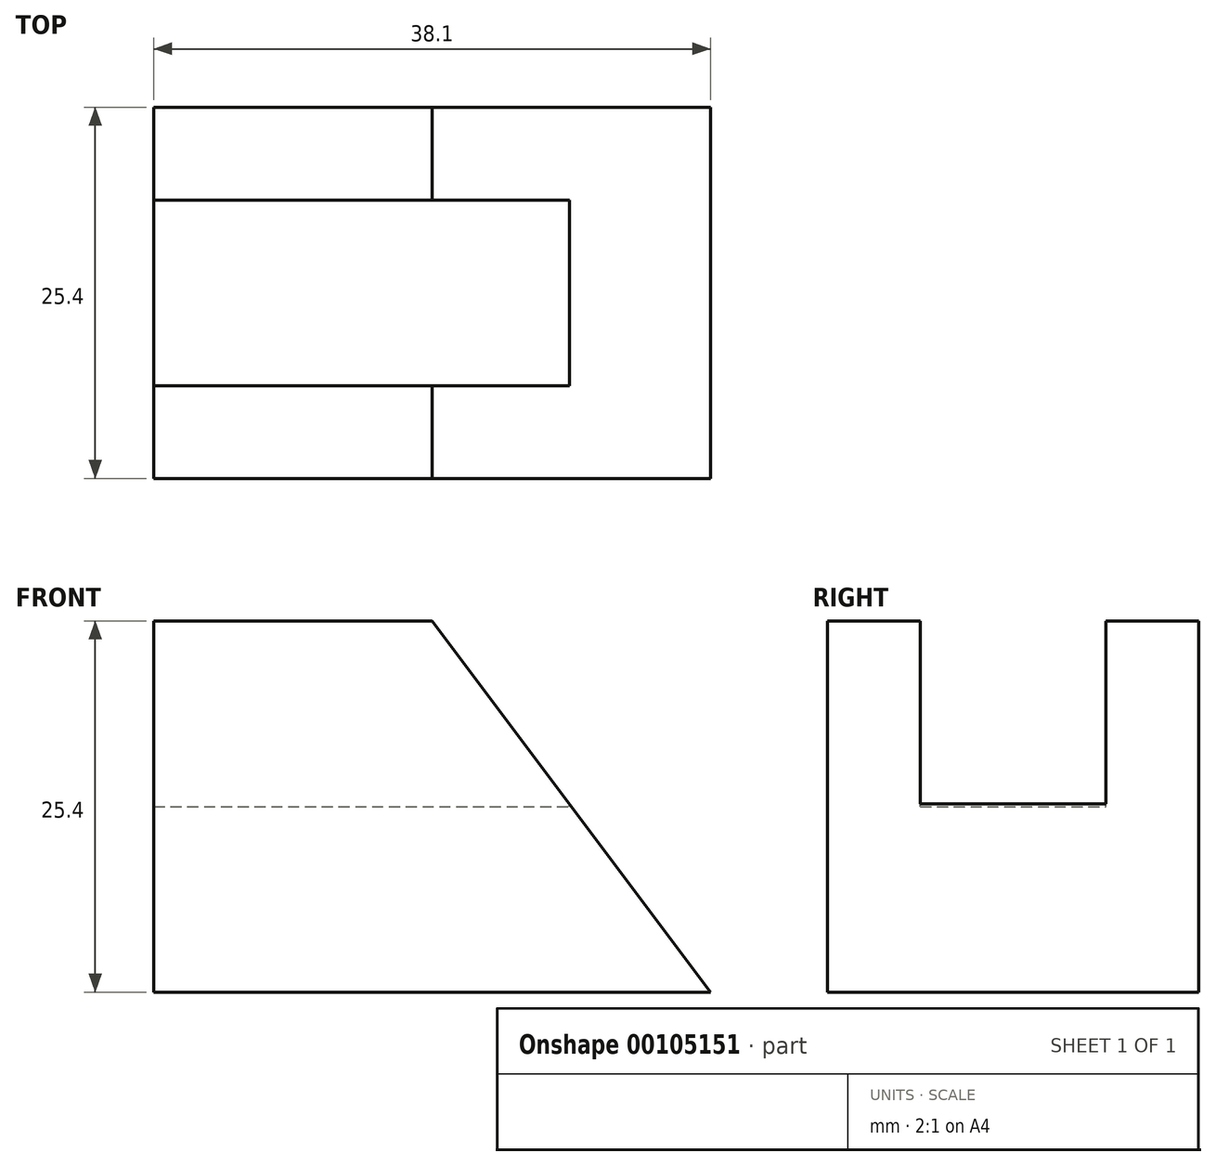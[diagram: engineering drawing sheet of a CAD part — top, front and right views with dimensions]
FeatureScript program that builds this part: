
annotation { "Feature Type Name" : "Feature", "Feature Type Description" : "" }
export const myFeature = defineFeature(function(context is Context, id is Id, definition is map)
    precondition{}
    {
        {
            var Q0;
            Q0=qCreatedBy(makeId("Front.planeOp"),FACE);
            var sketch = newSketch(context, id + "F0", { "sketchPlane" : qUnion([Q0])});
            skLineSegment(sketch, "E0", {"start": v(0, 0) * mm, "end": v(0, 25.4) * mm});
            skLineSegment(sketch, "E1", {"start": v(0, 25.4) * mm, "end": v(19.05, 25.4) * mm});
            skLineSegment(sketch, "E2", {"start": v(19.05, 25.4) * mm, "end": v(38.1, 0) * mm});
            skLineSegment(sketch, "E3", {"start": v(38.1, 0) * mm, "end": v(0, 0) * mm});
            skSolve(sketch);
        }
        {
            var Q0;
            Q0 = qSketchRegion(id + "F0", true);
            extrude(context, id + "F1", {"entities" : qUnion([Q0]), "depth" : 25.4 * mm});
        }
        {
            var Q0;
            Q0=makeQuery(id+"F1.opExtrude","SWEPT_FACE",FACE,{"disambiguationData":[OSD([sQuery(id+"F0.wireOp",EDGE,"E1")])]});
            var sketch = newSketch(context, id + "F2", { "sketchPlane" : qUnion([Q0])});
            skLineSegment(sketch, "E4.bottom", {"start": v(0, -6.35) * mm, "end": v(28.45, -6.35) * mm});
            skLineSegment(sketch, "E4.top", {"start": v(0, -19.05) * mm, "end": v(28.45, -19.05) * mm});
            skLineSegment(sketch, "E4.left", {"start": v(0, -6.35) * mm, "end": v(0, -19.05) * mm});
            skLineSegment(sketch, "E4.right", {"start": v(28.45, -6.35) * mm, "end": v(28.45, -19.05) * mm});
            skSolve(sketch);
        }
        {
            var Q0;
            Q0 = qSketchRegion(id + "F2", true);
            extrude(context, id + "F3", {"entities" : qUnion([Q0]), "operationType" : NewBodyOperationType.REMOVE, "oppositeDirection" : true, "depth" : 12.7 * mm});
        }
    });
